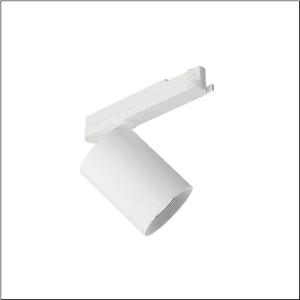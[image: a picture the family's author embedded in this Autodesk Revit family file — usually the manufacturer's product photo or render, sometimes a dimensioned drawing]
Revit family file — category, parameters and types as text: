
# Revit family: spot_11_51sd15mbb5a
name_source: partatom
category: Lighting Fixtures
units: mm (PartAtom-declared; Revit-internal decimal feet)

## family parameters
Cut with Voids When Loaded = No
Host = Face
Light Source = No
Part Type = Normal
Room Calculation Point = No
Round Connector Dimension = Use Diameter
Shared = No

## types (1)
- --- (1 x LED, 7370 lm, 50.2 W, 3000K)
    Apparent Load = 50 VA
    CIE Flux Codes = 91 98 100 100 100
    Color Rendering = 90
    Color Temperature = 3000K
    Default Elevation = 1800 mm
    Description = Spot 11, directional spotlight, light control with lens, of PMMA, LED rated luminous flux: 5.750lm, light colour: 930, control gear: ECG Multilumen, with 3-phase adapter, mains connection: 220..240V, AC, 50/60Hz, of aluminium, traffic white (RAL 9016), length: 213mm, diameter: 105mm, protection rating (complete): IP20, insulation class (complete): insulation class I (protective earthing), certification: CE, impact resistance: IK02, permissible ambient temperature for indoor applications: -20..+40°C, packaging unit: 1 piece
    Height = 175 mm
    Lamp = 1 x LED
    Lamp Light Flux = 7370 lm
    Lamp Power = 50.2 W
    Lamp count = 1
    Length = 105 mm
    Luminous efficacy = 147 lm/W
    Manufacturer = Siteco
    ModVariant = No
    Model = 51SD15MBB5A
    Mounting Place = Ceiling
    Mounting Type = Pendant
    Number of Poles = 1
    OnlyDefault = Yes
    Power Factor = 1
    Product Name = Spot 11
    Product group = directional spotlight
    ProductGroupID = 905
    Protection Class = Protection class I
    Protection Degree = IP 20
    RLX_Detail_Level = 1
    RLX_Emergency_Light_Flux = 0 lm
    RLX_Emergency_Type = 0
    RLX_Emergency_Type_DB = No
    RlxData = <blob elided: 17737 chars, md5=1cd2a0a2>
    Socket = socket
    Standby Power = 0 W
    System Light Flux = 7370 lm
    System Power = 50 W
    Type Comments = factory setting: luminous flux: 100 % | (ON | ON | ON | ON) | 1050 mA
    Type Image = l_1006697.jpg
    URL = http://relux.com
    VarID = @adj_097127
    Voltage = 0 V
    Weight = 0.00 kg
    Width = 0 mm  [stored 0 ft]

note: [stored X ft] marks values corroborated as IEEE doubles in the binary element streams (Revit-internal decimal feet)

## geometry (parser evidence)
native form markers: Blend x4, Sweep x9
no freeform markers — native parametric forms only
